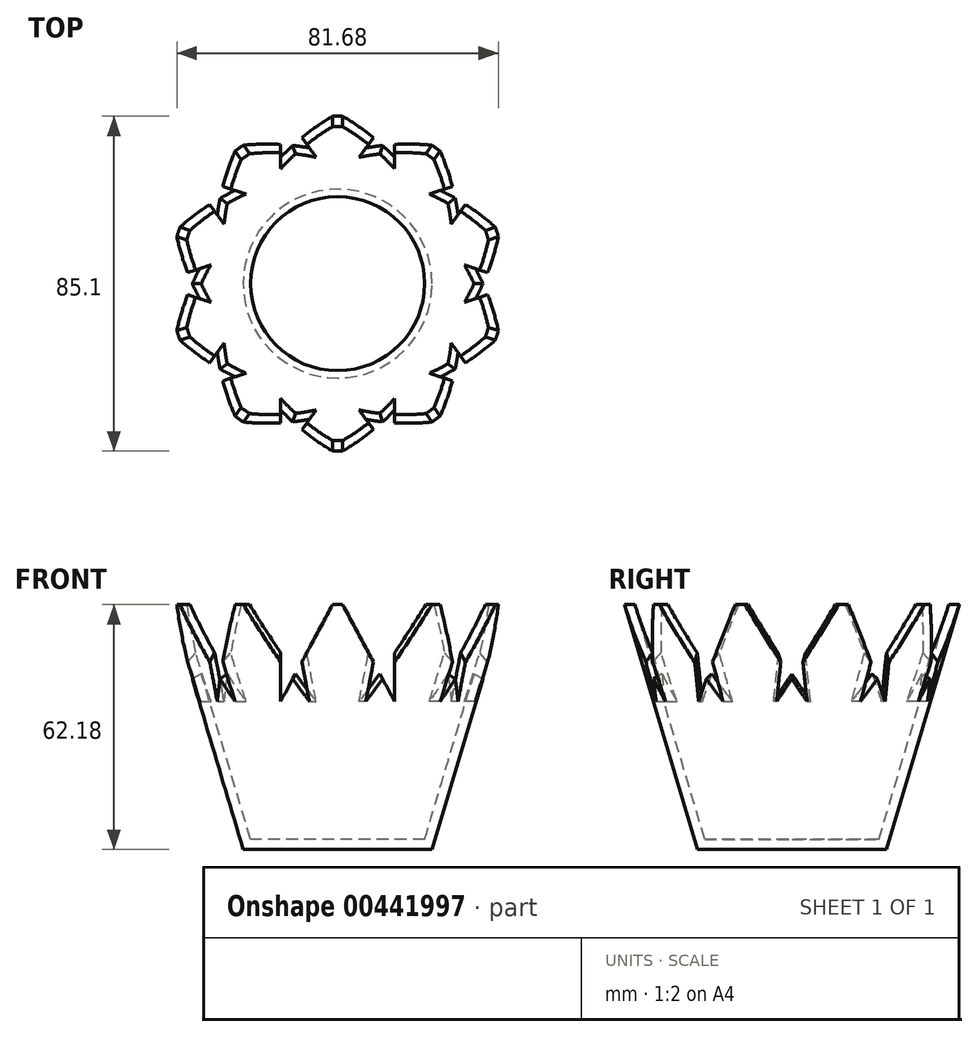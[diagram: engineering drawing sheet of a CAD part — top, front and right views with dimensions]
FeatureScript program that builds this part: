
annotation { "Feature Type Name" : "Feature", "Feature Type Description" : "" }
export const myFeature = defineFeature(function(context is Context, id is Id, definition is map)
    precondition{}
    {
        {
            var Q0;
            Q0=qCreatedBy(makeId("Front.planeOp"),FACE);
            var sketch = newSketch(context, id + "F0", { "sketchPlane" : qUnion([Q0])});
            skLineSegment(sketch, "E0", {"start": v(0, 0) * mm, "end": v(0, 62.18) * mm});
            skLineSegment(sketch, "E1", {"start": v(0, 62.18) * mm, "end": v(-42.55, 62.18) * mm});
            skLineSegment(sketch, "E2", {"start": v(-42.55, 62.18) * mm, "end": v(-24, 0) * mm});
            skLineSegment(sketch, "E3", {"start": v(-24, 0) * mm, "end": v(0, 0) * mm});
            skSolve(sketch);
        }
        {
            var Q0;
            Q0=makeQuery(id+"F0.imprint","IMPRINT",FACE,{"disambiguationData":[TD([[makeQuery(id+"F0.imprint","IMPRINT",EDGE,{"derivedFrom":sQuery(id+"F0.wireOp",EDGE,"E0")}),1.0]])]});
            var Q1;
            Q1=sQuery(id+"F0.wireOp",EDGE,"E0");
            revolve(context, id + "F1", {"entities" : qUnion([Q0]), "axis" : qUnion([Q1]), "revolveType" : RevolveType.FULL});
        }
        {
            var Q0;
            Q0=makeQuery(id+"F1.opRevolve","SWEPT_FACE",FACE,{"disambiguationData":[OSD([sQuery(id+"F0.wireOp",EDGE,"E1")])]});
            shell(context, id + "F2", {"entities" : qUnion([Q0]), "thickness" : 2.54 * mm});
        }
        {
            var Q0;
            Q0=qCreatedBy(makeId("Front.planeOp"),FACE);
            var sketch = newSketch(context, id + "F3", { "sketchPlane" : qUnion([Q0])});
            skLineSegment(sketch, "E4", {"start": v(0, 64.59) * mm, "end": v(0, 9.68) * mm});
            skLineSegment(sketch, "E5", {"start": v(0, 64.59) * mm, "end": v(-14.46, 37.6) * mm});
            skLineSegment(sketch, "E6.MirrorCS", {"start": v(0, 64.59) * mm, "end": v(14.46, 37.6) * mm});
            skLineSegment(sketch, "E7", {"start": v(14.46, 37.6) * mm, "end": v(14.46, 68.2) * mm, "construction": true});
            skLineSegment(sketch, "E8", {"start": v(14.46, 68.2) * mm, "end": v(-14.46, 68.2) * mm, "construction": true});
            skLineSegment(sketch, "E9", {"start": v(-14.46, 37.6) * mm, "end": v(-14.46, 68.2) * mm, "construction": true});
            skLineSegment(sketch, "E10", {"start": v(14.46, 37.6) * mm, "end": v(14.46, 68.2) * mm});
            skLineSegment(sketch, "E11", {"start": v(-14.46, 68.2) * mm, "end": v(-14.46, 37.6) * mm});
            skLineSegment(sketch, "E12", {"start": v(-14.46, 68.2) * mm, "end": v(14.46, 68.2) * mm});
            skSolve(sketch);
        }
        {
            var Q0;
            Q0 = qSketchRegion(id + "F3", true);
            extrude(context, id + "F4", {"entities" : qUnion([Q0]), "endBound" : BoundingType.THROUGH_ALL, "depth" : 47.5 * mm, "offsetDistance" : 25.4 * mm});
        }
        {
            var Q0;
            Q0=makeQuery(id+"F4.opExtrude","SWEPT_BODY",BODY,{"disambiguationData":[OSD([sQuery(id+"F3.wireOp",EDGE,"E5"),sQuery(id+"F3.wireOp",EDGE,"E6.MirrorCS"),sQuery(id+"F3.wireOp",EDGE,"E10"),sQuery(id+"F3.wireOp",EDGE,"E11"),sQuery(id+"F3.wireOp",EDGE,"E12")])]});
            var Q1;
            Q1=makeQuery(id+"F2.opShell","OFFSET_FACE",FACE,{"disambiguationData":[OSD([sQuery(id+"F0.wireOp",EDGE,"E2")])]});
            circularPattern(context, id + "F5", {"operationType" : NewBodyOperationType.REMOVE, "entities" : qUnion([Q0]), "axis" : qUnion([Q1]), "angle" : 360 * degree, "instanceCount" : 10, "equalSpace" : true});
        }
    });
